# Revit family: AWD
name_source: partatom
category: Mechanical Equipment
units: mm (PartAtom-declared; Revit-internal decimal feet)

## family parameters
Always vertical = Yes
Cut with Voids When Loaded = No
Part Type = Normal
Room Calculation Point = No
Round Connector Dimension = Use Diameter
Shared = No
Work Plane-Based = No

## types (8) — shared parameters
.125 = 1/8"
.5" = 1/2"
0 = 0"
1" = 1"
1.5 = 1 1/2"
130 = 130.00°
2" = 2"
2' = 24"
3" = 3"
4" = 4"
9" = 9"
92 = 92.00°
Manufacturer = Loren Cook Company
Model = AWD
Type Comments = Wall Exhaust Fan Cast Aluminum Propeller Direct Drive
URL = www.lorencook.com

## per-type parameters (varying)
- 12_AWD: (A/2)-1"=7 27/32"; (A/2)-C-.5"=4 11/32"; (SIZE/2)-.25"=5 3/4"; -((A/2)-C-.5")=-4 11/32"; -((SIZE/2)-.25")=-5 3/4"; -B=-15 3/8"; -B+1"=-14 3/8"; -C/2=-1 5/8"; -D=-2"; -WC_D=-14 5/16"; -WG_A=-12 9/16"; -WH_B/2=-11"; A=16 3/16"; A/2=8 3/32"; A/3.5=4 5/8"; A/7=2 5/16"; B=15 3/8"; B/2=7 11/16"; C=3 1/4"; C/2=1 5/8"; D=2"; D/2=1"; SIZE=12"; SIZE/2=6"; WC_A=16 3/16"; WC_B=19 1/2"; WC_C=14 3/8"; WG_B=17"; WG_C=1"; WG_D=12 9/16"; WH_A=18 11/16"; WH_B=22"; WH_B/2=11"
- 16_AWD: (A/2)-1"=9 27/32"; (A/2)-C-.5"=5 3/32"; (SIZE/2)-.25"=7 3/4"; -((A/2)-C-.5")=-5 3/32"; -((SIZE/2)-.25")=-7 3/4"; -B=-14 1/8"; -B+1"=-13 1/8"; -C/2=-2 1/4"; -D=-2"; -WC_D=-15 5/16"; -WG_A=-12 9/16"; -WH_B/2=-13"; A=20 3/16"; A/2=10 3/32"; A/3.5=5 25/32"; A/7=2 7/8"; B=14 1/8"; B/2=7 1/16"; C=4 1/2"; C/2=2 1/4"; D=2"; D/2=1"; SIZE=16"; SIZE/2=8"; WC_A=20 3/16"; WC_B=23 1/2"; WC_C=18 3/8"; WG_B=21"; WG_C=1"; WG_D=12 9/16"; WH_A=21 11/16"; WH_B=26"; WH_B/2=13"
- 20_AWD: (A/2)-1"=11 27/32"; (A/2)-C-.5"=6 11/32"; (SIZE/2)-.25"=9 3/4"; -((A/2)-C-.5")=-6 11/32"; -((SIZE/2)-.25")=-9 3/4"; -B=-14 1/8"; -B+1"=-13 1/8"; -C/2=-2 5/8"; -D=-2"; -WC_D=-17 1/2"; -WG_A=-12 9/16"; -WH_B/2=-15"; A=24 3/16"; A/2=12 3/32"; A/3.5=6 29/32"; A/7=3 15/32"; B=14 1/8"; B/2=7 1/16"; C=5 1/4"; C/2=2 5/8"; D=2"; D/2=1"; SIZE=20"; SIZE/2=10"; WC_A=24 1/4"; WC_B=27 1/2"; WC_C=22 3/8"; WG_B=25"; WG_C=1"; WG_D=12 9/16"; WH_A=24 3/8"; WH_B=30"; WH_B/2=15"
- 24_AWD: (A/2)-1"=14 27/32"; (A/2)-C-.5"=7 27/32"; (SIZE/2)-.25"=11 3/4"; -((A/2)-C-.5")=-7 27/32"; -((SIZE/2)-.25")=-11 3/4"; -B=-14 5/8"; -B+1"=-13 5/8"; -C/2=-3 3/8"; -D=-2"; -WC_D=-18 11/16"; -WG_A=-20 9/16"; -WH_B/2=-17"; A=30 3/16"; A/2=15 3/32"; A/3.5=8 5/8"; A/7=4 5/16"; B=14 5/8"; B/2=7 5/16"; C=6 3/4"; C/2=3 3/8"; D=2"; D/2=1"; SIZE=24"; SIZE/2=12"; WC_A=30 1/4"; WC_B=33 9/16"; WC_C=28 7/16"; WG_B=31"; WG_C=1 1/2"; WG_D=12 9/16"; WH_A=27 1/8"; WH_B=34"; WH_B/2=17"
- 30_AWD: (A/2)-1"=17 27/32"; (A/2)-C-.5"=10 27/32"; (SIZE/2)-.25"=14 3/4"; -((A/2)-C-.5")=-10 27/32"; -((SIZE/2)-.25")=-14 3/4"; -B=-14 5/8"; -B+1"=-13 5/8"; -C/2=-3 3/8"; -D=-3"; -WC_D=-18 11/16"; -WG_A=-20 9/16"; -WH_B/2=-20"; A=36 3/16"; A/2=18 3/32"; A/3.5=10 11/32"; A/7=5 5/32"; B=14 5/8"; B/2=7 5/16"; C=6 3/4"; C/2=3 3/8"; D=3"; D/2=1 1/2"; SIZE=30"; SIZE/2=15"; WC_A=36 1/4"; WC_B=39 9/16"; WC_C=34 7/16"; WG_B=37"; WG_C=1 1/2"; WG_D=12 9/16"; WH_A=31 7/16"; WH_B=40"; WH_B/2=20"
- 36_AWD: (A/2)-1"=20 27/32"; (A/2)-C-.5"=13 7/32"; (SIZE/2)-.25"=17 3/4"; -((A/2)-C-.5")=-13 7/32"; -((SIZE/2)-.25")=-17 3/4"; -B=-22"; -B+1"=-21"; -C/2=-3 11/16"; -D=-3"; -WC_D=-19 7/16"; -WG_A=-20 9/16"; -WH_B/2=-23"; A=42 3/16"; A/2=21 3/32"; A/3.5=12 1/16"; A/7=6 1/32"; B=22"; B/2=11"; C=7 3/8"; C/2=3 11/16"; D=3"; D/2=1 1/2"; SIZE=36"; SIZE/2=18"; WC_A=42 1/4"; WC_B=45 9/16"; WC_C=40 1/2"; WG_B=43"; WG_C=1 1/2"; WG_D=12 9/16"; WH_A=35 11/16"; WH_B=46"; WH_B/2=23"
- 42_AWD: (A/2)-1"=23 27/32"; (A/2)-C-.5"=15 31/32"; (SIZE/2)-.25"=20 3/4"; -((A/2)-C-.5")=-15 31/32"; -((SIZE/2)-.25")=-20 3/4"; -B=-24"; -B+1"=-23"; -C/2=-3 13/16"; -D=-3"; -WC_D=-19 7/16"; -WG_A=-25 9/16"; -WH_B/2=-26"; A=48 3/16"; A/2=24 3/32"; A/3.5=13 25/32"; A/7=6 7/8"; B=24"; B/2=12"; C=7 5/8"; C/2=3 13/16"; D=3"; D/2=1 1/2"; SIZE=42"; SIZE/2=21"; WC_A=48 1/4"; WC_B=51 5/8"; WC_C=46 1/2"; WG_B=49"; WG_C=1 1/2"; WG_D=12 9/16"; WH_A=39 15/16"; WH_B=52"; WH_B/2=26"
- 48_AWD: (A/2)-1"=26 27/32"; (A/2)-C-.5"=18 31/32"; (SIZE/2)-.25"=23 3/4"; -((A/2)-C-.5")=-18 31/32"; -((SIZE/2)-.25")=-23 3/4"; -B=-24"; -B+1"=-23"; -C/2=-3 13/16"; -D=-3"; -WC_D=-19 11/16"; -WG_A=-28 7/16"; -WH_B/2=-29"; A=54 3/16"; A/2=27 3/32"; A/3.5=15 15/32"; A/7=7 3/4"; B=24"; B/2=12"; C=7 5/8"; C/2=3 13/16"; D=3"; D/2=1 1/2"; SIZE=48"; SIZE/2=24"; WC_A=54 1/4"; WC_B=57 5/8"; WC_C=52 1/2"; WG_B=55"; WG_C=1 1/2"; WG_D=13 7/16"; WH_A=44 3/16"; WH_B=58"; WH_B/2=29"

## geometry (parser evidence)
native form markers: Sweep x2
no freeform markers — native parametric forms only
